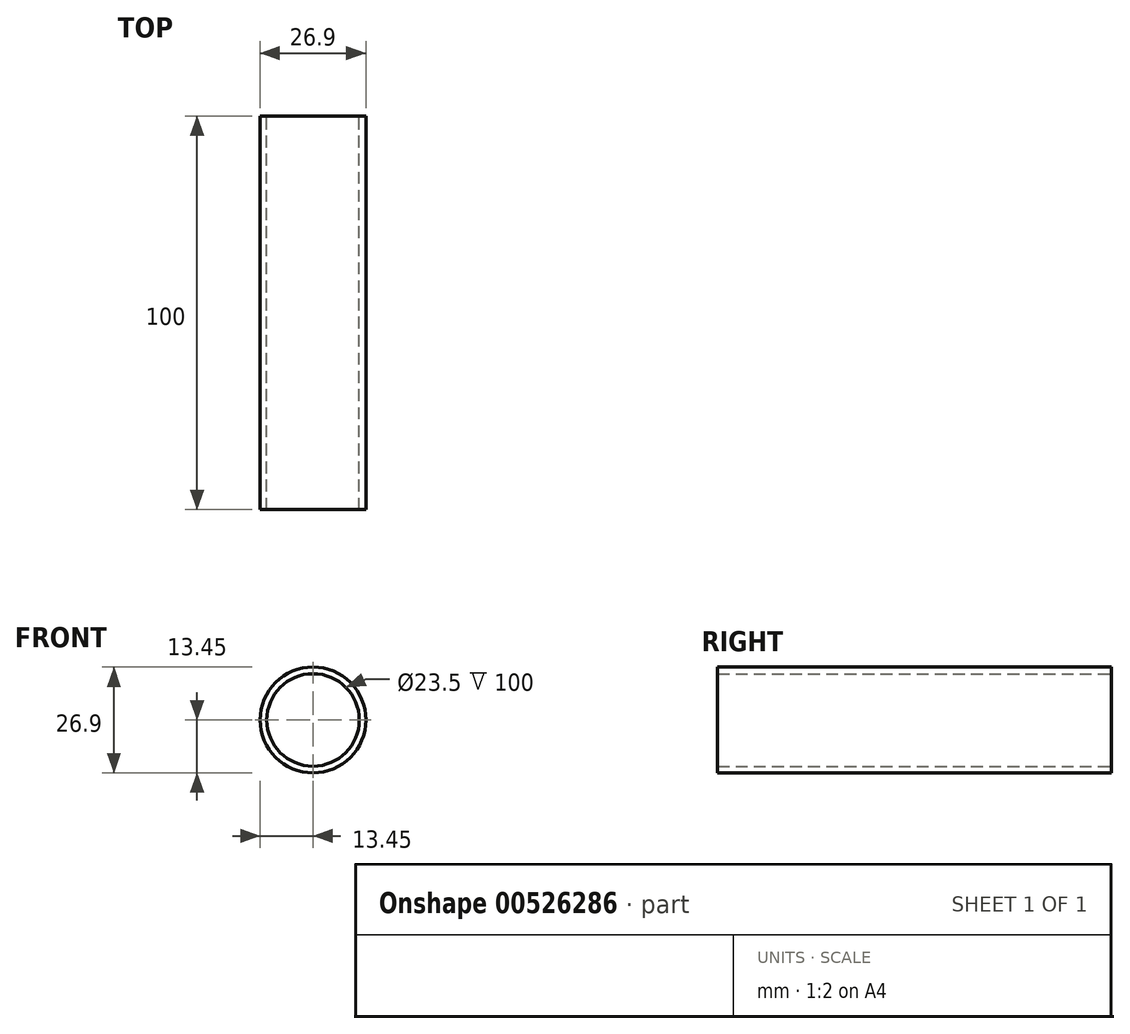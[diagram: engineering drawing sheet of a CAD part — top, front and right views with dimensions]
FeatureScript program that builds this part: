
annotation { "Feature Type Name" : "Feature", "Feature Type Description" : "" }
export const myFeature = defineFeature(function(context is Context, id is Id, definition is map)
    precondition{}
    {
        {
            var Q0;
            Q0=qCreatedBy(makeId("Front.planeOp"),FACE);
            var sketch = newSketch(context, id + "F0", { "sketchPlane" : qUnion([Q0])});
            skCircle(sketch, "E0", {"center": v(0, 0) * mm, "radius": 13.45 * mm});
            skCircle(sketch, "E1", {"center": v(0, 0) * mm, "radius": 11.75 * mm});
            skSolve(sketch);
        }
        {
            var Q0;
            Q0=qSketchRegion(id+"F0",true);
            extrude(context, id + "F1", {"entities" : qUnion([Q0]), "depth" : 100 * mm, "offsetDistance" : 25 * mm});
        }
    });
